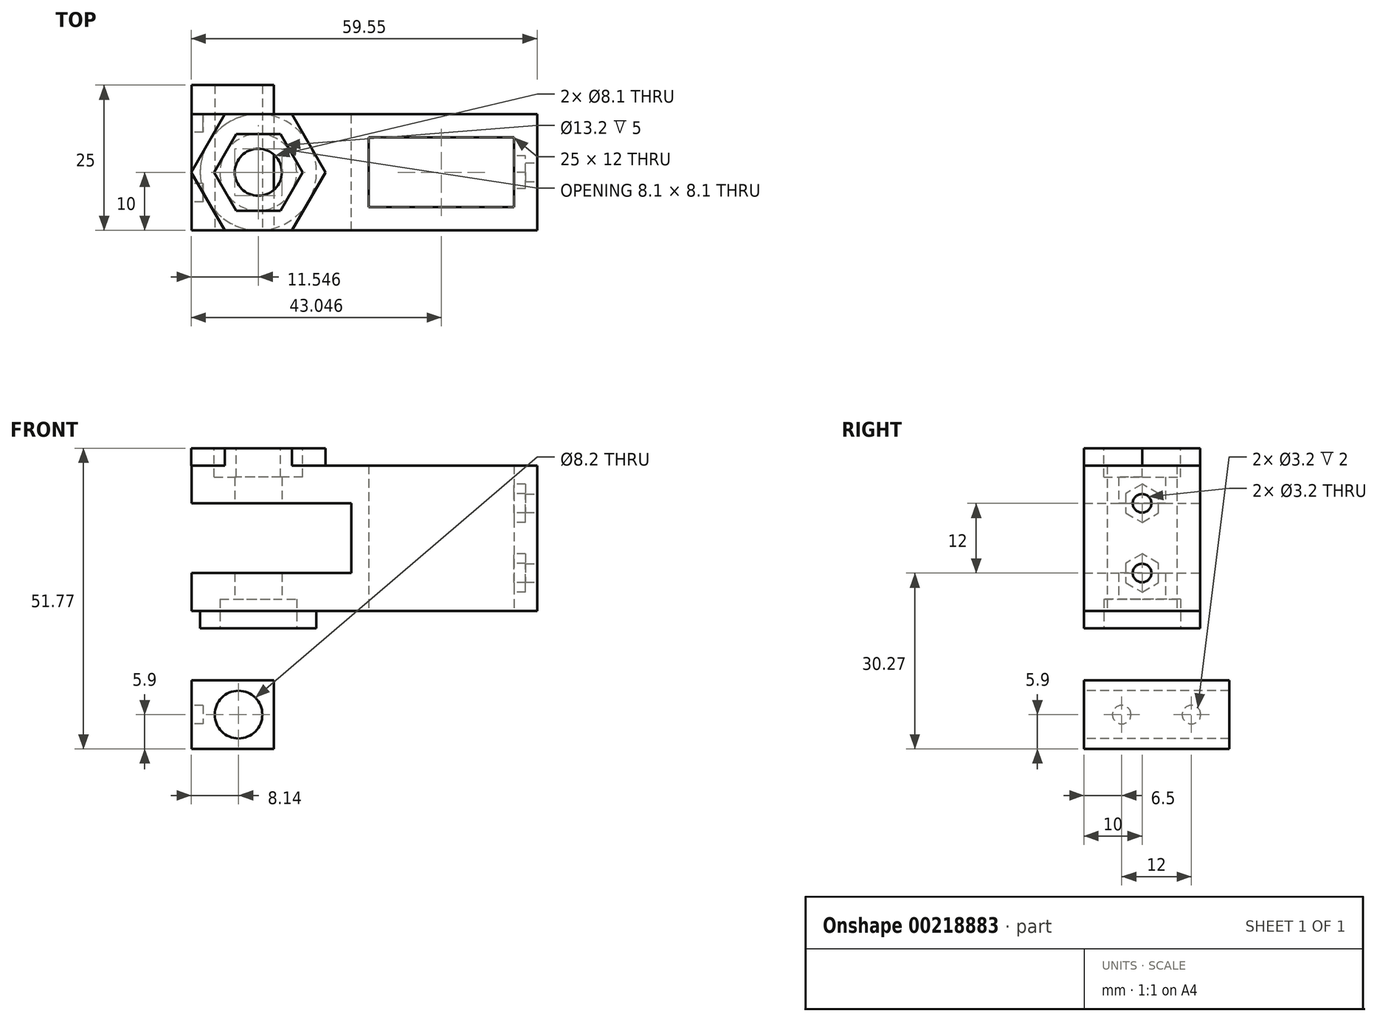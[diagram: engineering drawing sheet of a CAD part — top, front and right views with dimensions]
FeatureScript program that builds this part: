
annotation { "Feature Type Name" : "Feature", "Feature Type Description" : "" }
export const myFeature = defineFeature(function(context is Context, id is Id, definition is map)
    precondition{}
    {
        {
            var Q0;
            Q0=qCreatedBy(makeId("Top.planeOp"),FACE);
            var sketch = newSketch(context, id + "F0", { "sketchPlane" : qUnion([Q0])});
            skLineSegment(sketch, "E0.bottom", {"start": v(0, 0) * mm, "end": v(59.5, 0) * mm});
            skLineSegment(sketch, "E0.top", {"start": v(0, 20) * mm, "end": v(59.5, 20) * mm});
            skLineSegment(sketch, "E0.left", {"start": v(0, 0) * mm, "end": v(0, 20) * mm});
            skLineSegment(sketch, "E0.right", {"start": v(59.5, 0) * mm, "end": v(59.5, 20) * mm});
            skCircle(sketch, "E1", {"center": v(11.5, 10) * mm, "radius": 4.05 * mm});
            skCircle(sketch, "E2", {"center": v(11.5, 10) * mm, "radius": 16 * mm, "construction": true});
            skLineSegment(sketch, "E3.bottom", {"start": v(30.5, 16) * mm, "end": v(55.5, 16) * mm});
            skLineSegment(sketch, "E3.top", {"start": v(30.5, 4) * mm, "end": v(55.5, 4) * mm});
            skLineSegment(sketch, "E3.left", {"start": v(30.5, 16) * mm, "end": v(30.5, 4) * mm});
            skLineSegment(sketch, "E3.right", {"start": v(55.5, 16) * mm, "end": v(55.5, 4) * mm});
            skCircle(sketch, "E4.cCircle", {"center": v(11.5, 10) * mm, "radius": 6.5 * mm, "construction": true});
            skLineSegment(sketch, "E4.0", {"start": v(4, 10) * mm, "end": v(7.75, 16.5) * mm, "construction": true});
            skLineSegment(sketch, "E4.1", {"start": v(7.75, 16.5) * mm, "end": v(15.26, 16.5) * mm, "construction": true});
            skLineSegment(sketch, "E4.2", {"start": v(15.26, 16.5) * mm, "end": v(19.01, 10) * mm, "construction": true});
            skLineSegment(sketch, "E4.3", {"start": v(19.01, 10) * mm, "end": v(15.26, 3.5) * mm, "construction": true});
            skLineSegment(sketch, "E4.4", {"start": v(15.26, 3.5) * mm, "end": v(7.75, 3.5) * mm, "construction": true});
            skLineSegment(sketch, "E4.5", {"start": v(7.75, 3.5) * mm, "end": v(4, 10) * mm, "construction": true});
            skPoint(sketch, "E4.0.midPoint", {"position": v(5.88, 13.25) * mm});
            skSolve(sketch);
        }
        {
            var Q0;
            Q0=makeQuery(id+"F0.imprint","IMPRINT",FACE,{"disambiguationData":[TD([[makeQuery(id+"F0.imprint","IMPRINT",EDGE,{"derivedFrom":sQuery(id+"F0.wireOp",EDGE,"E0.bottom")}),1.0]])]});
            extrude(context, id + "F1", {"entities" : qUnion([Q0]), "depth" : 25 * mm});
        }
        {
            var Q0;
            Q0=makeQuery(id+"F1.opExtrude","SWEPT_FACE",FACE,{"disambiguationData":[OSD([sQuery(id+"F0.wireOp",EDGE,"E0.top")])]});
            var sketch = newSketch(context, id + "F2", { "sketchPlane" : qUnion([Q0])});
            skLineSegment(sketch, "E5", {"start": v(0, 0) * mm, "end": v(0, 6.5) * mm, "construction": true});
            skLineSegment(sketch, "E6", {"start": v(0, 6.5) * mm, "end": v(-27.5, 6.5) * mm});
            skLineSegment(sketch, "E7", {"start": v(-27.5, 6.5) * mm, "end": v(-27.5, 18.5) * mm});
            skLineSegment(sketch, "E8", {"start": v(-27.5, 18.5) * mm, "end": v(0, 18.5) * mm});
            skLineSegment(sketch, "E9", {"start": v(0, 25) * mm, "end": v(0, 18.5) * mm, "construction": true});
            skLineSegment(sketch, "E10", {"start": v(0, 18.5) * mm, "end": v(0, 6.5) * mm});
            skSolve(sketch);
        }
        {
            var Q0;
            Q0 = qSketchRegion(id + "F2", true);
            extrude(context, id + "F3", {"entities" : qUnion([Q0]), "operationType" : NewBodyOperationType.REMOVE, "oppositeDirection" : true, "depth" : 25 * mm});
        }
        {
            var Q0;
            Q0=makeQuery(id+"F1.opExtrude","CAP_FACE",FACE,{"disambiguationData":[OSD([sQuery(id+"F0.wireOp",EDGE,"E0.bottom"),sQuery(id+"F0.wireOp",EDGE,"E0.top"),sQuery(id+"F0.wireOp",EDGE,"E0.left"),sQuery(id+"F0.wireOp",EDGE,"E0.right"),sQuery(id+"F0.wireOp",EDGE,"E1"),sQuery(id+"F0.wireOp",EDGE,"E3.bottom"),sQuery(id+"F0.wireOp",EDGE,"E3.top"),sQuery(id+"F0.wireOp",EDGE,"E3.left"),sQuery(id+"F0.wireOp",EDGE,"E3.right")])],"isStart":false});
            var sketch = newSketch(context, id + "F4", { "sketchPlane" : qUnion([Q0])});
            skCircle(sketch, "E11.cCircle", {"center": v(11.5, 10) * mm, "radius": 10 * mm, "construction": true});
            skLineSegment(sketch, "E11.0", {"start": v(5.73, 20) * mm, "end": v(17.28, 20) * mm});
            skLineSegment(sketch, "E11.1", {"start": v(17.28, 20) * mm, "end": v(23.05, 10) * mm});
            skLineSegment(sketch, "E11.2", {"start": v(23.05, 10) * mm, "end": v(17.28, 0) * mm});
            skLineSegment(sketch, "E11.3", {"start": v(17.28, 0) * mm, "end": v(5.73, 0) * mm});
            skLineSegment(sketch, "E11.4", {"start": v(5.73, 0) * mm, "end": v(-0.04, 10) * mm});
            skLineSegment(sketch, "E11.5", {"start": v(-0.04, 10) * mm, "end": v(5.73, 20) * mm});
            skPoint(sketch, "E11.0.midPoint", {"position": v(11.5, 20) * mm});
            skSolve(sketch);
        }
        {
            var Q0;
            Q0 = qSketchRegion(id + "F4", true);
            extrude(context, id + "F5", {"entities" : qUnion([Q0]), "operationType" : NewBodyOperationType.ADD, "depth" : 3 * mm});
        }
        {
            var Q0;
            Q0=makeQuery(id+"F5.opExtrude","CAP_FACE",FACE,{"disambiguationData":[OSD([sQuery(id+"F4.wireOp",EDGE,"E11.0"),sQuery(id+"F4.wireOp",EDGE,"E11.1"),sQuery(id+"F4.wireOp",EDGE,"E11.2"),sQuery(id+"F4.wireOp",EDGE,"E11.3"),sQuery(id+"F4.wireOp",EDGE,"E11.4"),sQuery(id+"F4.wireOp",EDGE,"E11.5")])],"isStart":false});
            var sketch = newSketch(context, id + "F6", { "sketchPlane" : qUnion([Q0])});
            skCircle(sketch, "E12.cCircle", {"center": v(11.5, 10) * mm, "radius": 6.6 * mm, "construction": true});
            skLineSegment(sketch, "E12.0", {"start": v(3.88, 10) * mm, "end": v(7.7, 16.6) * mm});
            skLineSegment(sketch, "E12.1", {"start": v(7.7, 16.6) * mm, "end": v(15.32, 16.6) * mm});
            skLineSegment(sketch, "E12.2", {"start": v(15.32, 16.6) * mm, "end": v(19.13, 10) * mm});
            skLineSegment(sketch, "E12.3", {"start": v(19.13, 10) * mm, "end": v(15.32, 3.4) * mm});
            skLineSegment(sketch, "E12.4", {"start": v(15.32, 3.4) * mm, "end": v(7.7, 3.4) * mm});
            skLineSegment(sketch, "E12.5", {"start": v(7.7, 3.4) * mm, "end": v(3.88, 10) * mm});
            skPoint(sketch, "E12.0.midPoint", {"position": v(5.79, 13.3) * mm});
            skLineSegment(sketch, "E13", {"start": v(-0.04, 10) * mm, "end": v(3.88, 10) * mm, "construction": true});
            skLineSegment(sketch, "E14", {"start": v(15.32, 3.4) * mm, "end": v(17.28, 0) * mm, "construction": true});
            skLineSegment(sketch, "E15", {"start": v(15.32, 16.6) * mm, "end": v(17.28, 20) * mm, "construction": true});
            skSolve(sketch);
        }
        {
            var Q0;
            Q0 = qSketchRegion(id + "F6", true);
            extrude(context, id + "F7", {"entities" : qUnion([Q0]), "operationType" : NewBodyOperationType.REMOVE, "oppositeDirection" : true, "depth" : 5 * mm});
        }
        {
            var Q0;
            Q0=makeQuery(id+"F1.opExtrude","CAP_FACE",FACE,{"disambiguationData":[OSD([sQuery(id+"F0.wireOp",EDGE,"E0.bottom"),sQuery(id+"F0.wireOp",EDGE,"E0.top"),sQuery(id+"F0.wireOp",EDGE,"E0.left"),sQuery(id+"F0.wireOp",EDGE,"E0.right"),sQuery(id+"F0.wireOp",EDGE,"E1"),sQuery(id+"F0.wireOp",EDGE,"E3.bottom"),sQuery(id+"F0.wireOp",EDGE,"E3.top"),sQuery(id+"F0.wireOp",EDGE,"E3.left"),sQuery(id+"F0.wireOp",EDGE,"E3.right")])],"isStart":true});
            var sketch = newSketch(context, id + "F8", { "sketchPlane" : qUnion([Q0])});
            skCircle(sketch, "E16", {"center": v(11.5, -10) * mm, "radius": 10 * mm});
            skSolve(sketch);
        }
        {
            var Q0;
            Q0 = qSketchRegion(id + "F8", true);
            extrude(context, id + "F9", {"entities" : qUnion([Q0]), "operationType" : NewBodyOperationType.ADD, "depth" : 3 * mm});
        }
        {
            var Q0;
            Q0=makeQuery(id+"F9.opExtrude","CAP_FACE",FACE,{"disambiguationData":[OSD([sQuery(id+"F8.wireOp",EDGE,"E16")])],"isStart":false});
            var sketch = newSketch(context, id + "F10", { "sketchPlane" : qUnion([Q0])});
            skCircle(sketch, "E17", {"center": v(11.5, -10) * mm, "radius": 6.6 * mm});
            skSolve(sketch);
        }
        {
            var Q0;
            Q0=makeQuery(id+"F10.imprint","IMPRINT",FACE,{"disambiguationData":[TD([[makeQuery(id+"F10.imprint","IMPRINT",EDGE,{"derivedFrom":sQuery(id+"F10.wireOp",EDGE,"E17")}),1.0]])]});
            var Q1;
            Q1=sQuery(id+"F10.wireOp",EDGE,"E17");
            extrude(context, id + "F11", {"entities" : qUnion([Q0]), "operationType" : NewBodyOperationType.REMOVE, "surfaceEntities" : qUnion([Q1]), "oppositeDirection" : true, "depth" : 5 * mm});
        }
        {
            var Q0;
            Q0=makeQuery(id+"F1.opExtrude","SWEPT_FACE",FACE,{"disambiguationData":[OSD([sQuery(id+"F0.wireOp",EDGE,"E0.right")])]});
            var sketch = newSketch(context, id + "F12", { "sketchPlane" : qUnion([Q0])});
            skLineSegment(sketch, "E18", {"start": v(10, 0) * mm, "end": v(10, 25) * mm, "construction": true});
            skCircle(sketch, "E19", {"center": v(10, 6.5) * mm, "radius": 1.6 * mm});
            skCircle(sketch, "E20", {"center": v(10, 18.5) * mm, "radius": 1.6 * mm});
            skLineSegment(sketch, "E21", {"start": v(10, 6.5) * mm, "end": v(10, 0) * mm, "construction": true});
            skLineSegment(sketch, "E22", {"start": v(10, 25) * mm, "end": v(10, 18.5) * mm, "construction": true});
            skSolve(sketch);
        }
        {
            var Q0;
            Q0 = qSketchRegion(id + "F12", true);
            extrude(context, id + "F13", {"entities" : qUnion([Q0]), "operationType" : NewBodyOperationType.REMOVE, "endBound" : BoundingType.UP_TO_NEXT, "oppositeDirection" : true, "depth" : 25 * mm});
        }
        {
            var Q0;
            Q0=qCreatedBy(makeId("Front.planeOp"),FACE);
            var sketch = newSketch(context, id + "F14", { "sketchPlane" : qUnion([Q0])});
            skLineSegment(sketch, "E23.bottom", {"start": v(0, -11.97) * mm, "end": v(14.2, -11.97) * mm});
            skLineSegment(sketch, "E23.top", {"start": v(0, -23.77) * mm, "end": v(14.2, -23.77) * mm});
            skLineSegment(sketch, "E23.left", {"start": v(0, -11.97) * mm, "end": v(0, -23.77) * mm});
            skLineSegment(sketch, "E24", {"start": v(14.2, -17.87) * mm, "end": v(0, -17.87) * mm, "construction": true});
            skCircle(sketch, "E25", {"center": v(8.1, -17.87) * mm, "radius": 4.1 * mm});
            skLineSegment(sketch, "E26", {"start": v(14.2, -11.97) * mm, "end": v(14.2, -23.77) * mm});
            skSolve(sketch);
        }
        {
            var Q0;
            Q0 = qSketchRegion(id + "F14", true);
            extrude(context, id + "F15", {"entities" : qUnion([Q0]), "oppositeDirection" : true, "depth" : 25 * mm});
        }
        {
            var Q0;
            Q0=makeQuery(id+"F15.opExtrude","SWEPT_FACE",FACE,{"disambiguationData":[OSD([sQuery(id+"F14.wireOp",EDGE,"E23.left")])]});
            var sketch = newSketch(context, id + "F16", { "sketchPlane" : qUnion([Q0])});
            skLineSegment(sketch, "E27", {"start": v(-25, -17.87) * mm, "end": v(0, -17.87) * mm, "construction": true});
            skLineSegment(sketch, "E28", {"start": v(-6.5, -17.87) * mm, "end": v(0, -17.87) * mm, "construction": true});
            skLineSegment(sketch, "E29", {"start": v(-25, -17.87) * mm, "end": v(-18.5, -17.87) * mm, "construction": true});
            skCircle(sketch, "E30", {"center": v(-18.5, -17.87) * mm, "radius": 1.6 * mm});
            skCircle(sketch, "E31", {"center": v(-6.5, -17.87) * mm, "radius": 1.6 * mm});
            skSolve(sketch);
        }
        {
            var Q0;
            Q0 = qSketchRegion(id + "F16", true);
            extrude(context, id + "F17", {"entities" : qUnion([Q0]), "operationType" : NewBodyOperationType.REMOVE, "oppositeDirection" : true, "depth" : 2 * mm});
        }
        {
            var Q0;
            Q0=makeQuery(id+"F1.opExtrude","SWEPT_FACE",FACE,{"disambiguationData":[OSD([sQuery(id+"F0.wireOp",EDGE,"E3.right")])]});
            var sketch = newSketch(context, id + "F18", { "sketchPlane" : qUnion([Q0])});
            skCircle(sketch, "E32.cCircle", {"center": v(-10, 6.5) * mm, "radius": 2.85 * mm, "construction": true});
            skLineSegment(sketch, "E32.0", {"start": v(-12.85, 4.85) * mm, "end": v(-12.85, 8.15) * mm});
            skLineSegment(sketch, "E32.1", {"start": v(-12.85, 8.15) * mm, "end": v(-10, 9.8) * mm});
            skLineSegment(sketch, "E32.2", {"start": v(-10, 9.8) * mm, "end": v(-7.15, 8.15) * mm});
            skLineSegment(sketch, "E32.3", {"start": v(-7.15, 8.15) * mm, "end": v(-7.15, 4.85) * mm});
            skLineSegment(sketch, "E32.4", {"start": v(-7.15, 4.85) * mm, "end": v(-10, 3.2) * mm});
            skLineSegment(sketch, "E32.5", {"start": v(-10, 3.2) * mm, "end": v(-12.85, 4.85) * mm});
            skPoint(sketch, "E32.0.midPoint", {"position": v(-12.85, 6.5) * mm});
            skCircle(sketch, "E33.cCircle", {"center": v(-10, 18.5) * mm, "radius": 2.85 * mm, "construction": true});
            skLineSegment(sketch, "E33.0", {"start": v(-12.85, 16.85) * mm, "end": v(-12.85, 20.15) * mm});
            skLineSegment(sketch, "E33.1", {"start": v(-12.85, 20.15) * mm, "end": v(-10, 21.8) * mm});
            skLineSegment(sketch, "E33.2", {"start": v(-10, 21.8) * mm, "end": v(-7.15, 20.15) * mm});
            skLineSegment(sketch, "E33.3", {"start": v(-7.15, 20.15) * mm, "end": v(-7.15, 16.85) * mm});
            skLineSegment(sketch, "E33.4", {"start": v(-7.15, 16.85) * mm, "end": v(-10, 15.2) * mm});
            skLineSegment(sketch, "E33.5", {"start": v(-10, 15.2) * mm, "end": v(-12.85, 16.85) * mm});
            skPoint(sketch, "E33.0.midPoint", {"position": v(-12.85, 18.5) * mm});
            skSolve(sketch);
        }
        {
            var Q0;
            Q0 = qSketchRegion(id + "F18", true);
            extrude(context, id + "F19", {"entities" : qUnion([Q0]), "operationType" : NewBodyOperationType.REMOVE, "oppositeDirection" : true, "depth" : 2 * mm});
        }
    });
